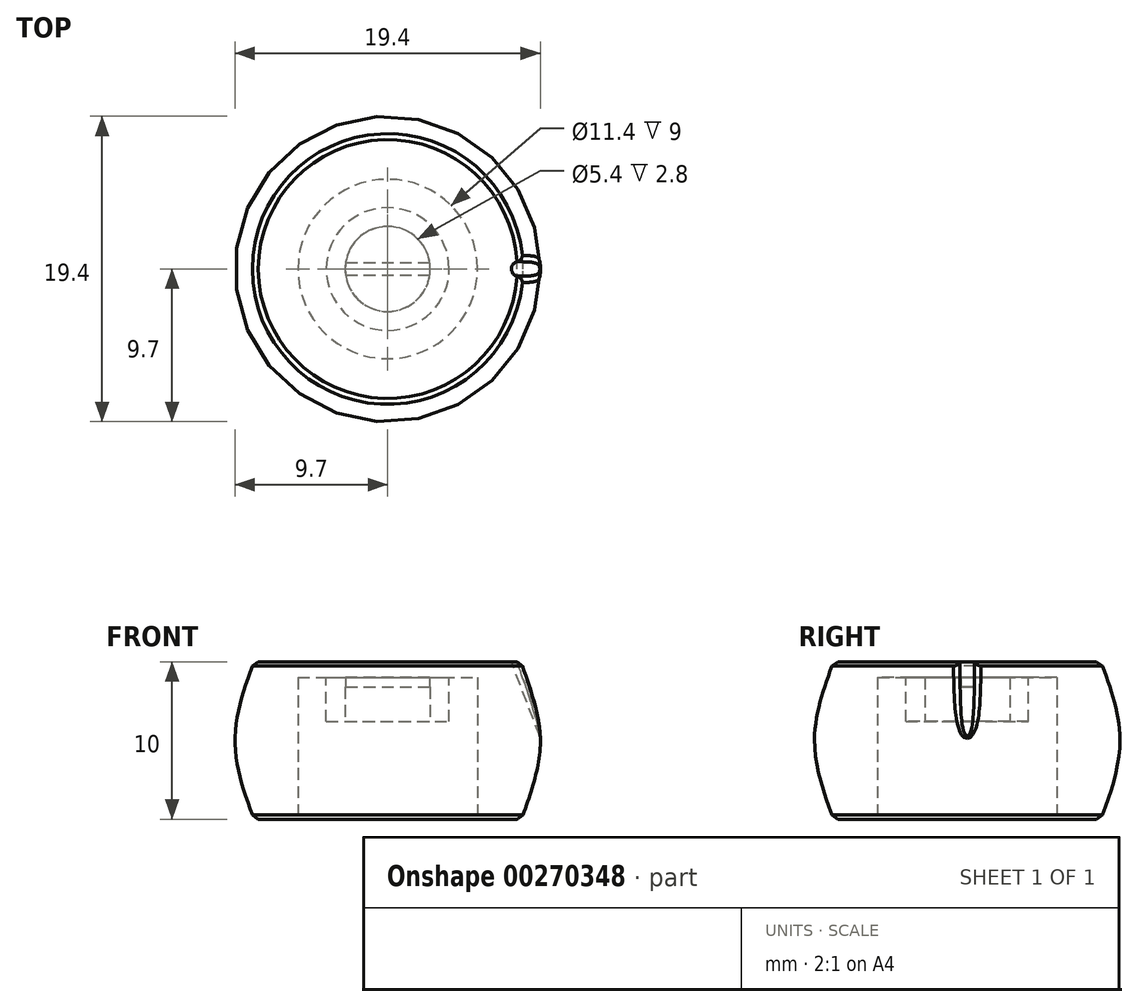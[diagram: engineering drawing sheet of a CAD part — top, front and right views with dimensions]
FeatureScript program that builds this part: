
annotation { "Feature Type Name" : "Feature", "Feature Type Description" : "" }
export const myFeature = defineFeature(function(context is Context, id is Id, definition is map)
    precondition{}
    {
        {
            var Q0;
            Q0=qCreatedBy(makeId("Front.planeOp"),FACE);
            var sketch = newSketch(context, id + "F0", { "sketchPlane" : qUnion([Q0])});
            skLineSegment(sketch, "E0.bottom", {"start": v(-8.5, 5) * mm, "end": v(8.5, 5) * mm});
            skLineSegment(sketch, "E0.top", {"start": v(-8.5, -5) * mm, "end": v(8.5, -5) * mm});
            skLineSegment(sketch, "E0.left", {"start": v(-8.5, 5) * mm, "end": v(-8.5, -5) * mm});
            skLineSegment(sketch, "E0.right", {"start": v(8.5, 5) * mm, "end": v(8.5, -5) * mm, "construction": true});
            skPoint(sketch, "E0.middle", {"position": v(0, 0) * mm});
            skLineSegment(sketch, "E1", {"start": v(0, 5) * mm, "end": v(0, -5) * mm});
            skLineSegment(sketch, "E2", {"start": v(0, 0) * mm, "end": v(9.7, 0) * mm, "construction": true});
            skFitSpline(sketch, "E3", {"points": [v(8.5, 5) * mm, v(9.7, 0) * mm, v(8.5, -5) * mm], "startDerivative": vector(3.6, -10) * mm, "endDerivative": vector(-3.6, -10) * mm});
            skSolve(sketch);
        }
        {
            var Q0;
            {var subQ2=sQuery(id+"F0.wireOp",EDGE,"E1");Q0=makeQuery(id+"F0.imprint","IMPRINT",FACE,{"disambiguationData":[TD([[makeQuery(id+"F0.imprint","IMPRINT",EDGE,{"derivedFrom":subQ2}),1.0]])]});}
            var Q1;
            Q1=sQuery(id+"F0.wireOp",EDGE,"E1");
            revolve(context, id + "F1", {"entities" : qUnion([Q0]), "axis" : qUnion([Q1]), "revolveType" : RevolveType.FULL});
        }
        {
            var Q0;
            Q0=qCreatedBy(makeId("Front.planeOp"),FACE);
            var sketch = newSketch(context, id + "F2", { "sketchPlane" : qUnion([Q0])});
            skLineSegment(sketch, "E4.0", {"start": v(-8.5, 5) * mm, "end": v(8.5, 5) * mm});
            skLineSegment(sketch, "E5", {"start": v(8.5, 5) * mm, "end": v(10.42, 0) * mm});
            skLineSegment(sketch, "E6", {"start": v(10.42, 0) * mm, "end": v(9.86, -0.22) * mm});
            skLineSegment(sketch, "E7", {"start": v(9.86, -0.22) * mm, "end": v(7.65, 5.54) * mm});
            skLineSegment(sketch, "E8", {"start": v(7.65, 5.54) * mm, "end": v(8.5, 5) * mm});
            skSolve(sketch);
        }
        {
            var Q0;
            Q0=makeQuery(id+"F1.opRevolve","SWEPT_EDGE",EDGE,{"disambiguationData":[OSD([sQuery(id+"F0.wireOp",EDGE,"E0.bottom"),sQuery(id+"F0.wireOp",EDGE,"E3")])]});
            var Q1;
            Q1=makeQuery(id+"F1.opRevolve","SWEPT_EDGE",EDGE,{"disambiguationData":[OSD([sQuery(id+"F0.wireOp",EDGE,"E0.top"),sQuery(id+"F0.wireOp",EDGE,"E3")])]});
            chamfer(context, id + "F3", {"entities" : qUnion([Q0, Q1]), "width" : 0.4 * mm, "tangentPropagation" : true});
        }
        {
            var Q0;
            Q0 = qSketchRegion(id + "F2", true);
            extrude(context, id + "F4", {"entities" : qUnion([Q0]), "operationType" : NewBodyOperationType.REMOVE, "depth" : 0.5 * mm, "hasSecondDirection" : true, "secondDirectionOppositeDirection" : true, "secondDirectionDepth" : 0.5 * mm});
        }
        {
            var Q0;
            Q0=makeQuery(id+"F4.boolean.opBoolean","COPY",EDGE,{"derivedFrom":makeQuery(id+"F4.opExtrude","CAP_EDGE",EDGE,{"disambiguationData":[OSD([sQuery(id+"F2.wireOp",EDGE,"E7")])],"isStart":true})});
            var Q1;
            Q1=makeQuery(id+"F4.boolean.opBoolean","COPY",EDGE,{"derivedFrom":makeQuery(id+"F4.opExtrude","CAP_EDGE",EDGE,{"disambiguationData":[OSD([sQuery(id+"F2.wireOp",EDGE,"E7")])],"isStart":false})});
            fillet(context, id + "F5", {"entities" : qUnion([Q0, Q1]), "radius" : 0.5 * mm, "tangentPropagation" : true, "allowEdgeOverflow" : false});
        }
        {
            var Q0;
            Q0=makeQuery(id+"F4.boolean.opBoolean","INTERSECT",EDGE,{"derivedFrom":[makeQuery(id+"F1.opRevolve","SWEPT_FACE",FACE,{"disambiguationData":[OSD([sQuery(id+"F0.wireOp",EDGE,"E3")])]}),makeQuery(id+"F4.opExtrude","CAP_FACE",FACE,{"disambiguationData":[OSD([sQuery(id+"F2.wireOp",EDGE,"E5"),sQuery(id+"F2.wireOp",EDGE,"E6"),sQuery(id+"F2.wireOp",EDGE,"E7"),sQuery(id+"F2.wireOp",EDGE,"E8")])],"isStart":true})]});
            var Q1;
            Q1=makeQuery(id+"F4.boolean.opBoolean","INTERSECT",EDGE,{"derivedFrom":[makeQuery(id+"F1.opRevolve","SWEPT_FACE",FACE,{"disambiguationData":[OSD([sQuery(id+"F0.wireOp",EDGE,"E3")])]}),makeQuery(id+"F4.opExtrude","CAP_FACE",FACE,{"disambiguationData":[OSD([sQuery(id+"F2.wireOp",EDGE,"E5"),sQuery(id+"F2.wireOp",EDGE,"E6"),sQuery(id+"F2.wireOp",EDGE,"E7"),sQuery(id+"F2.wireOp",EDGE,"E8")])],"isStart":false})]});
            fillet(context, id + "F6", {"entities" : qUnion([Q0, Q1]), "radius" : 0.4 * mm, "tangentPropagation" : true, "allowEdgeOverflow" : false});
        }
        {
            var Q0;
            Q0=makeQuery(id+"F1.opRevolve","SWEPT_FACE",FACE,{"disambiguationData":[OSD([sQuery(id+"F0.wireOp",EDGE,"E0.top")])]});
            var sketch = newSketch(context, id + "F7", { "sketchPlane" : qUnion([Q0])});
            skCircle(sketch, "E9", {"center": v(0, 0) * mm, "radius": 5.7 * mm});
            skSolve(sketch);
        }
        {
            var Q0;
            Q0 = qSketchRegion(id + "F7", true);
            extrude(context, id + "F8", {"entities" : qUnion([Q0]), "operationType" : NewBodyOperationType.REMOVE, "oppositeDirection" : true, "depth" : 9 * mm});
        }
        {
            var Q0;
            Q0=makeQuery(id+"F8.boolean.opBoolean","COPY",FACE,{"derivedFrom":makeQuery(id+"F8.opExtrude","CAP_FACE",FACE,{"disambiguationData":[OSD([sQuery(id+"F7.wireOp",EDGE,"E9")])],"isStart":false})});
            var sketch = newSketch(context, id + "F9", { "sketchPlane" : qUnion([Q0])});
            skCircle(sketch, "E10", {"center": v(0, 0) * mm, "radius": 3.9 * mm});
            skSolve(sketch);
        }
        {
            var Q0;
            Q0 = qSketchRegion(id + "F9", true);
            extrude(context, id + "F10", {"entities" : qUnion([Q0]), "operationType" : NewBodyOperationType.ADD, "depth" : 2.8 * mm});
        }
        {
            var Q0;
            Q0=makeQuery(id+"F10.opExtrude","CAP_FACE",FACE,{"disambiguationData":[OSD([sQuery(id+"F9.wireOp",EDGE,"E10")])],"isStart":false});
            var sketch = newSketch(context, id + "F11", { "sketchPlane" : qUnion([Q0])});
            skCircle(sketch, "E11", {"center": v(0, 0) * mm, "radius": 2.7 * mm});
            skSolve(sketch);
        }
        {
            var Q0;
            Q0 = qSketchRegion(id + "F11", true);
            extrude(context, id + "F12", {"entities" : qUnion([Q0]), "operationType" : NewBodyOperationType.REMOVE, "oppositeDirection" : true, "depth" : 2.8 * mm});
        }
        {
            var Q0;
            Q0=makeQuery(id+"F12.boolean.opBoolean","COPY",FACE,{"derivedFrom":makeQuery(id+"F12.opExtrude","CAP_FACE",FACE,{"disambiguationData":[OSD([sQuery(id+"F11.wireOp",EDGE,"E11")])],"isStart":false})});
            var sketch = newSketch(context, id + "F13", { "sketchPlane" : qUnion([Q0])});
            skLineSegment(sketch, "E12.bottom", {"start": v(-3, 0.4) * mm, "end": v(3, 0.4) * mm});
            skLineSegment(sketch, "E12.top", {"start": v(-3, -0.4) * mm, "end": v(3, -0.4) * mm});
            skLineSegment(sketch, "E12.left", {"start": v(-3, 0.4) * mm, "end": v(-3, -0.4) * mm});
            skLineSegment(sketch, "E12.right", {"start": v(3, 0.4) * mm, "end": v(3, -0.4) * mm});
            skPoint(sketch, "E12.middle", {"position": v(0, 0) * mm});
            skSolve(sketch);
        }
        {
            var Q0;
            Q0 = qSketchRegion(id + "F13", true);
            extrude(context, id + "F14", {"entities" : qUnion([Q0]), "operationType" : NewBodyOperationType.ADD, "depth" : 0.6 * mm});
        }
    });
